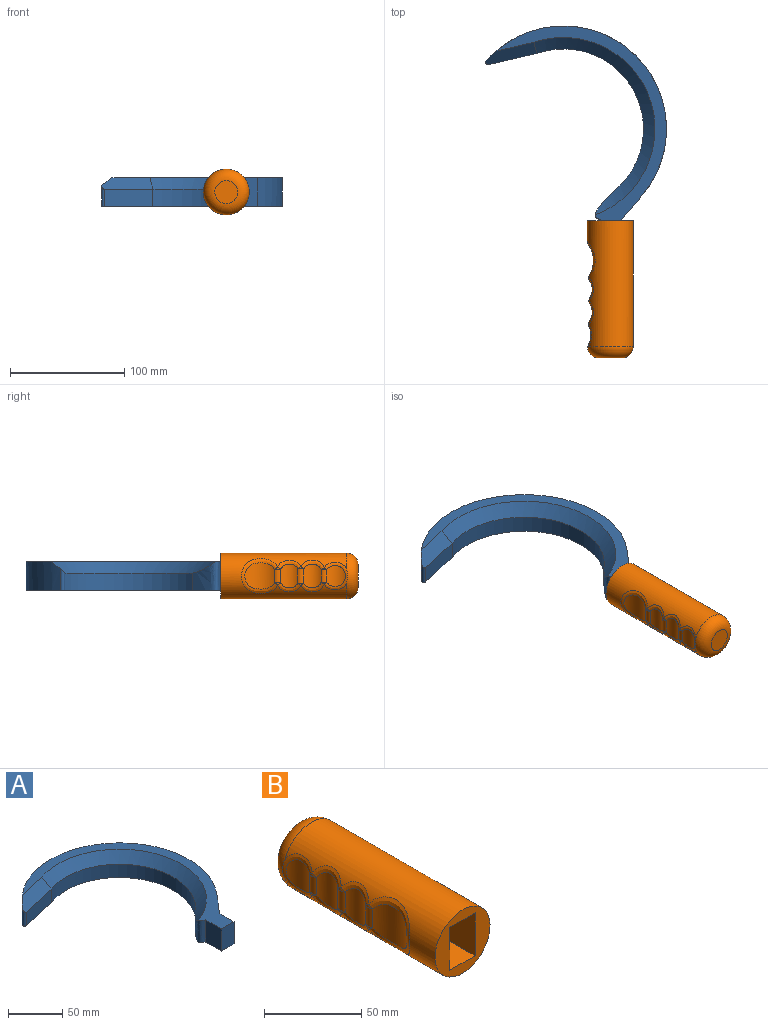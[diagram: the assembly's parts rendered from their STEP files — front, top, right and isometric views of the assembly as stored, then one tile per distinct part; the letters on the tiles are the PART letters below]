
ASSEMBLY  parts=2 mates=1
PART A: 13 faces, bbox 158.1x190x25 mm
  f0: plane 25x20.58mm, normal (-1,0,0), area 514.6mm2, adj f1,f7,f8,f9
  f1: plane 25x16.26mm, normal (0,-1,0), area 406.5mm2, adj f0,f2,f8,f9
  f2: plane 25x18.89mm, normal (1,0,0), area 472.2mm2, adj f1,f3,f8,f9
  f3: extruded ~25x22.64mm, area 744.4mm2, adj f2,f4,f8,f9
  f4: cylinder r=90mm len=157.53mm, axis (0,0,-1), area 6997.7mm2, adj f3,f8,f9,f11,f12
  f5: plane 42.44x15mm, normal (0.23,-0.97,0), area 653.5mm2, adj f6,f9,f11,f12
  f6: cylinder r=70mm len=125.21mm, axis (0,0,-1), area 2957.2mm2, adj f5,f7,f9,f10
  f7: extruded ~25x24.21mm, area 654.1mm2, adj f0,f6,f8,f9,f10
  f8: plane 190x148.92mm, normal (0,0,1), area 3206mm2, adj f0,f1,f2,f3,f4,f7,f10,f11
  f9: plane 190x158.03mm, normal (0,0,-1), area 5889.3mm2, adj f0,f1,f2,f3,f4,f5,f6,f7
  f10: cone r=70mm half-angle=45deg, axis (0,0,1), area 3207.8mm2, adj f6,f7,f8,f11
  f11: plane 44.92x19.54mm, normal (0.16,-0.69,0.71), area 587.2mm2, adj f4,f5,f8,f10,f12
  f12: cylinder r=2mm len=18.63mm, axis (0,0,-1), area 83.4mm2, adj f4,f5,f9,f11
PART B: 28 faces, bbox 43.3x120x43.3 mm
  f0: cylinder r=20mm len=110mm, axis (0,-1,0), area 11417.7mm2, adj f1,f14,f15,f19,f20,f24,f25,f27
  f1: plane 40x40mm, normal (0,-1,0), area 763.7mm2, adj f0,f3,f4,f5,f6
  f2: plane 20x20mm, normal (0,1,0), area 314.2mm2, adj f27
  f3: plane 20x18.26mm, normal (0,0,-1), area 365.2mm2, adj f1,f4,f6,f7
  f4: plane 27x20mm, normal (1,0,0), area 540mm2, adj f1,f3,f5,f7
  f5: plane 20x18.26mm, normal (0,0,1), area 365.2mm2, adj f1,f4,f6,f7
  f6: plane 27x20mm, normal (-1,0,0), area 540mm2, adj f1,f3,f5,f7
  f7: plane 27x18.26mm, normal (0,-1,0), area 493mm2, adj f3,f4,f5,f6
  f8: cylinder r=18mm len=18.09mm, axis (0,0,-1), area 255.9mm2, adj f13,f14
  f9: cylinder r=14mm len=20.82mm, axis (0,0,-1), area 288mm2, adj f18,f20,f23,f24
  f10: cylinder r=14mm len=20.82mm, axis (0,0,-1), area 291.3mm2, adj f13,f15,f18,f19
  f11: cylinder r=24mm len=26.02mm, axis (0,0,-1), area 523.5mm2, adj f23,f25
  f12: sphere r=5mm, area 5.6mm2, adj f13,f14,f15
  f13: cylinder r=5mm len=10.79mm, axis (0,0,1), area 54.6mm2, adj f8,f10,f12,f16
  f14: bspline ~24.13x21.4mm, area 158.3mm2, adj f0,f8,f12,f16,f27
  f15: bspline ~21.46x9.29mm, area 83.2mm2, adj f0,f10,f12,f17
  f16: sphere r=5mm, area 5.2mm2, adj f13,f14,f19
  f17: sphere r=5mm, area 7.9mm2, adj f15,f18,f20
  f18: cylinder r=5mm len=12.47mm, axis (0,0,-1), area 69.1mm2, adj f9,f10,f17,f21
  f19: bspline ~21.42x9.15mm, area 83.2mm2, adj f0,f10,f16,f21
  f20: bspline ~21.76x9.74mm, area 80.8mm2, adj f0,f9,f17,f22
  f21: sphere r=5mm, area 7.9mm2, adj f18,f19,f24
  f22: sphere r=5mm, area 5.8mm2, adj f20,f23,f25
  f23: cylinder r=5mm len=11.84mm, axis (0,0,1), area 65.3mm2, adj f9,f11,f22,f26
  f24: bspline ~21.42x9.15mm, area 80.8mm2, adj f0,f9,f21,f26
  f25: bspline ~32.4x30.44mm, area 300.9mm2, adj f0,f11,f22,f26
  f26: sphere r=5mm, area 6.5mm2, adj f23,f24,f25
  f27: torus R=10mm, axis (0,1,0), area 1608.2mm2, adj f0,f2,f14
PLACE A at identity
PLACE B rot(axis=(1,0,0),180deg) t=(149.9,-273.49,32.5)mm
MATE fastened B.f0 <-> A.f1  axis (0,1,0) through (40.94,-100,12.5)mm
